AUTODESK INVENTOR PART (.ipt)
format: ipt  version: 2015 (Build 190159000, 159)  size: 104,448 bytes
history: native  units: in
note: dims shown in document units (in); Inventor stores cm internally (conversion verified against a paired STEP export)
features: sketch x1
ambient origin geometry x8: Origin, YZ Plane, XZ Plane, XY Plane, X Axis, Y Axis, Z Axis, Center Point
feature tree (1):
  sketch  "Sketch1"  dims[d8=3.0in d19=0.5841in d29=0.75in d35=1.0in d36=0.2185in d39=2.594in d44=0.5in d45=1.844in d46=0.5in d47=1.75in d48=0.25in d49=105.0deg d50=0.5in d51=0.5in d52=0.25in d54=0.375in d56=2.0in d59=0.5in d60=0.25in d61=0.234in d64=0.25in d67=2.0in d68=0.25in d69=105.0deg d70=0.125in d71=0.25in d75=2.3995in d76=0.125in d77=0.25in d78=1.0in d80=0.1374in d82=1.675in d83=0.1443in d84=1.6531in d86=0.1718in d87=1.6531in d88=1.2713in d89=90.0deg d90=3.1729in]
